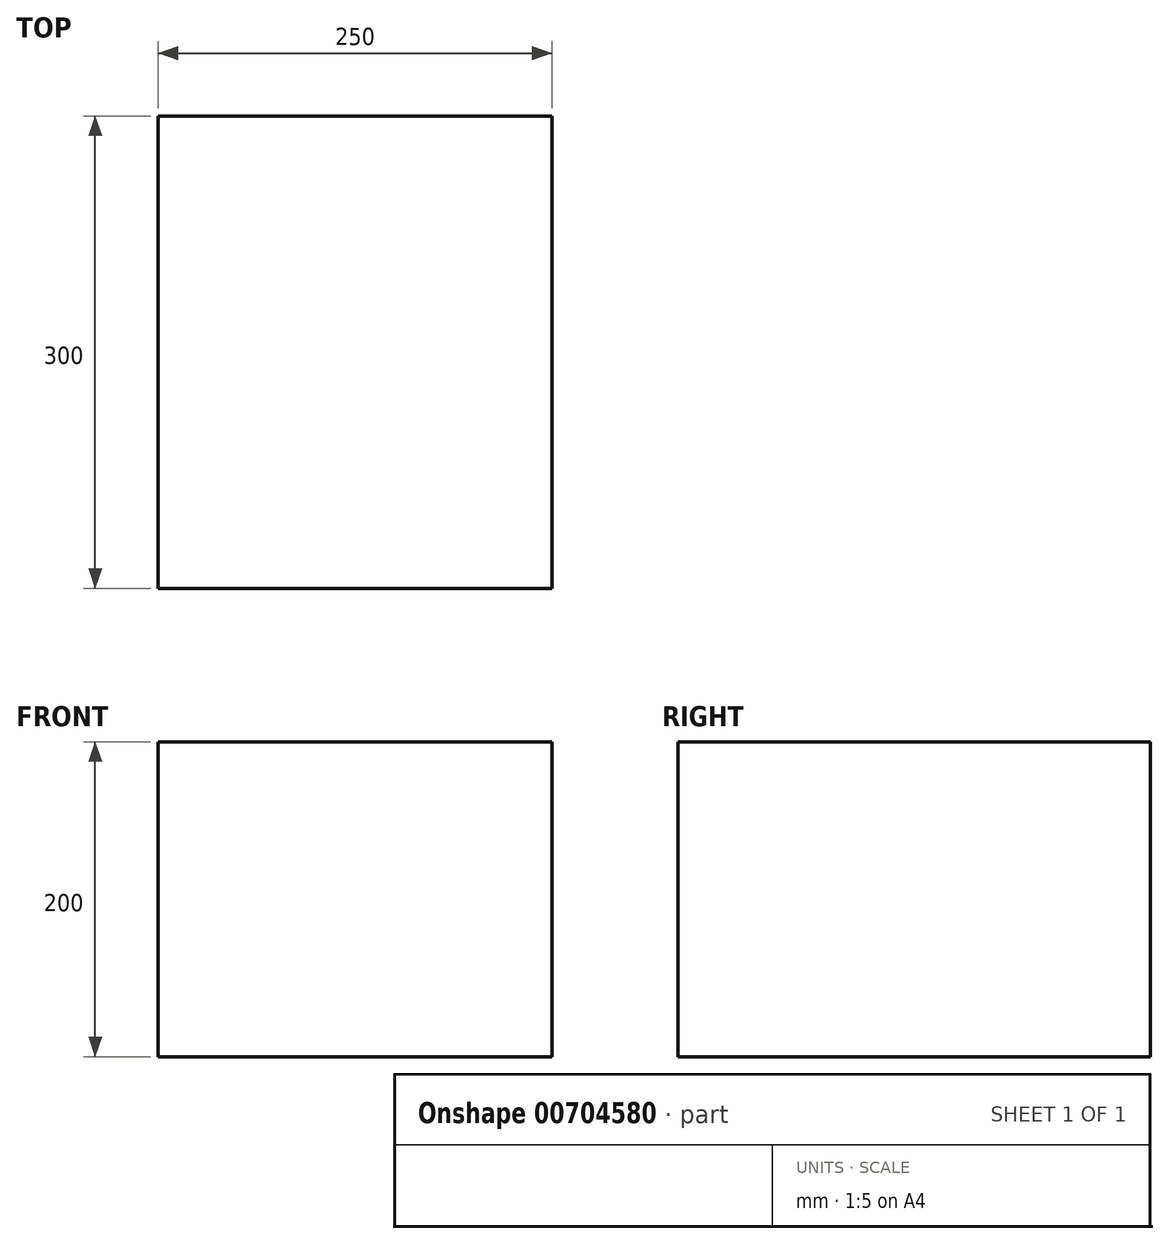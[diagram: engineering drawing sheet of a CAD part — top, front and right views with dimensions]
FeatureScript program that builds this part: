
annotation { "Feature Type Name" : "Feature", "Feature Type Description" : "" }
export const myFeature = defineFeature(function(context is Context, id is Id, definition is map)
    precondition{}
    {
        {
            var Q0;
            Q0=qCreatedBy(makeId("Top.planeOp"),FACE);
            var sketch = newSketch(context, id + "F0", { "sketchPlane" : qUnion([Q0])});
            skLineSegment(sketch, "E0.bottom", {"start": v(-250, 150) * mm, "end": v(0, 150) * mm});
            skLineSegment(sketch, "E0.top", {"start": v(-250, -150) * mm, "end": v(0, -150) * mm});
            skLineSegment(sketch, "E0.left", {"start": v(-250, 150) * mm, "end": v(-250, -150) * mm});
            skLineSegment(sketch, "E0.right", {"start": v(0, 150) * mm, "end": v(0, -150) * mm});
            skSolve(sketch);
        }
        {
            var Q0;
            Q0 = qSketchRegion(id + "F0", true);
            extrude(context, id + "F1", {"entities" : qUnion([Q0]), "endBound" : BoundingType.SYMMETRIC, "depth" : 200 * mm, "offsetDistance" : 25 * mm});
        }
    });
